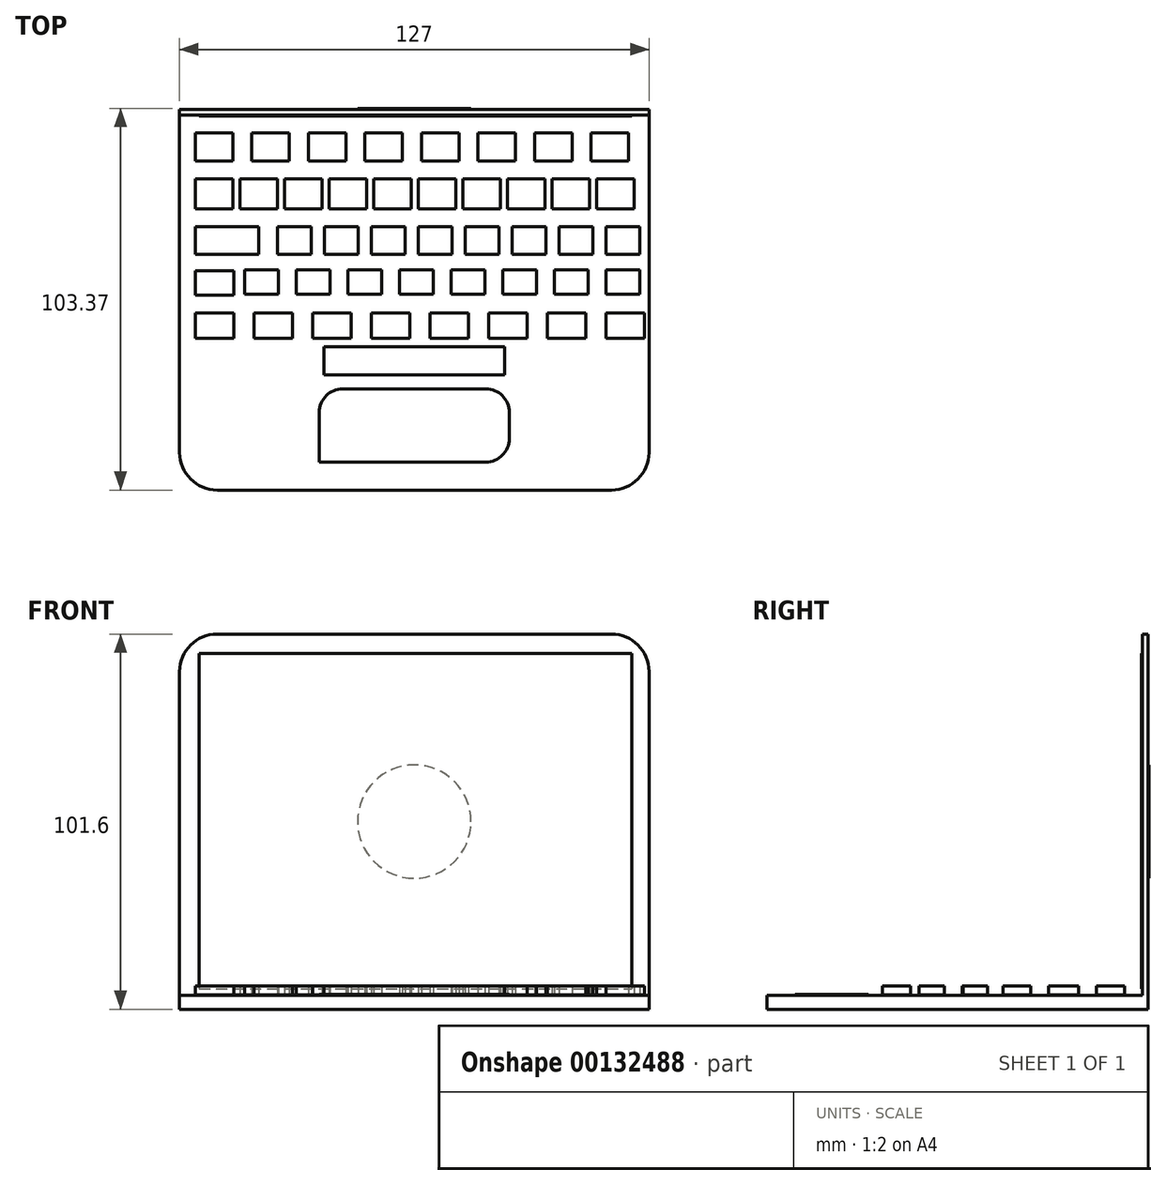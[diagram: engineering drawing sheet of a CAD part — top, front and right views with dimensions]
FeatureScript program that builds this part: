
annotation { "Feature Type Name" : "Feature", "Feature Type Description" : "" }
export const myFeature = defineFeature(function(context is Context, id is Id, definition is map)
    precondition{}
    {
        {
            var Q0;
            Q0=qCreatedBy(makeId("Front.planeOp"),FACE);
            var sketch = newSketch(context, id + "F0", { "sketchPlane" : qUnion([Q0])});
            skLineSegment(sketch, "E0.bottom", {"start": v(63.5, -50.8) * mm, "end": v(-63.5, -50.8) * mm});
            skLineSegment(sketch, "E0.top", {"start": v(63.5, 50.8) * mm, "end": v(-63.5, 50.8) * mm});
            skLineSegment(sketch, "E0.left", {"start": v(63.5, -50.8) * mm, "end": v(63.5, 50.8) * mm});
            skLineSegment(sketch, "E0.right", {"start": v(-63.5, -50.8) * mm, "end": v(-63.5, 50.8) * mm});
            skPoint(sketch, "E0.middle", {"position": v(0, 0) * mm});
            skSolve(sketch);
        }
        {
            var Q0;
            Q0 = qSketchRegion(id + "F0", true);
            extrude(context, id + "F1", {"entities" : qUnion([Q0]), "depth" : 1.52 * mm});
        }
        {
            var Q0;
            Q0=makeQuery(id+"F1.opExtrude","CAP_FACE",FACE,{"disambiguationData":[OSD([sQuery(id+"F0.wireOp",EDGE,"E0.bottom"),sQuery(id+"F0.wireOp",EDGE,"E0.top"),sQuery(id+"F0.wireOp",EDGE,"E0.left"),sQuery(id+"F0.wireOp",EDGE,"E0.right")])],"isStart":false});
            var sketch = newSketch(context, id + "F2", { "sketchPlane" : qUnion([Q0])});
            skLineSegment(sketch, "E1.bottom", {"start": v(-63.5, -50.8) * mm, "end": v(63.5, -50.8) * mm});
            skLineSegment(sketch, "E1.top", {"start": v(-63.5, -47) * mm, "end": v(63.5, -47) * mm});
            skLineSegment(sketch, "E1.left", {"start": v(-63.5, -50.8) * mm, "end": v(-63.5, -47) * mm});
            skLineSegment(sketch, "E1.right", {"start": v(63.5, -50.8) * mm, "end": v(63.5, -47) * mm});
            skSolve(sketch);
        }
        {
            var Q0;
            Q0 = qSketchRegion(id + "F2", true);
            extrude(context, id + "F3", {"entities" : qUnion([Q0]), "operationType" : NewBodyOperationType.ADD, "depth" : 101.6 * mm});
        }
        {
            var Q0;
            Q0=makeQuery(id+"F3.opExtrude","CAP_EDGE",EDGE,{"disambiguationData":[OSD([sQuery(id+"F2.wireOp",EDGE,"E1.left")])],"isStart":false});
            var Q1;
            Q1=makeQuery(id+"F3.opExtrude","CAP_EDGE",EDGE,{"disambiguationData":[OSD([sQuery(id+"F2.wireOp",EDGE,"E1.right")])],"isStart":false});
            var Q2;
            Q2=makeQuery(id+"F1.opExtrude","SWEPT_EDGE",EDGE,{"disambiguationData":[OSD([sQuery(id+"F0.wireOp",EDGE,"E0.top"),sQuery(id+"F0.wireOp",EDGE,"E0.right")])]});
            var Q3;
            Q3=makeQuery(id+"F1.opExtrude","SWEPT_EDGE",EDGE,{"disambiguationData":[OSD([sQuery(id+"F0.wireOp",EDGE,"E0.top"),sQuery(id+"F0.wireOp",EDGE,"E0.left")])]});
            fillet(context, id + "F4", {"entities" : qUnion([Q0, Q1, Q2, Q3]), "radius" : 10.16 * mm, "tangentPropagation" : true, "allowEdgeOverflow" : false});
        }
        {
            var Q0;
            Q0=makeQuery(id+"F1.opExtrude","CAP_FACE",FACE,{"disambiguationData":[OSD([sQuery(id+"F0.wireOp",EDGE,"E0.bottom"),sQuery(id+"F0.wireOp",EDGE,"E0.top"),sQuery(id+"F0.wireOp",EDGE,"E0.left"),sQuery(id+"F0.wireOp",EDGE,"E0.right")])],"isStart":false});
            var sketch = newSketch(context, id + "F5", { "sketchPlane" : qUnion([Q0])});
            skLineSegment(sketch, "E2.bottom", {"start": v(-58.24, 45.59) * mm, "end": v(58.8, 45.59) * mm});
            skLineSegment(sketch, "E2.top", {"start": v(-58.24, -45.21) * mm, "end": v(58.8, -45.21) * mm});
            skLineSegment(sketch, "E2.left", {"start": v(-58.24, 45.59) * mm, "end": v(-58.24, -45.21) * mm});
            skLineSegment(sketch, "E2.right", {"start": v(58.8, 45.59) * mm, "end": v(58.8, -45.21) * mm});
            skSolve(sketch);
        }
        {
            var Q0;
            Q0 = qSketchRegion(id + "F5", true);
            extrude(context, id + "F6", {"entities" : qUnion([Q0]), "depth" : 0.25 * mm});
        }
        {
            var Q0;
            Q0=makeQuery(id+"F3.opExtrude","SWEPT_FACE",FACE,{"disambiguationData":[OSD([sQuery(id+"F2.wireOp",EDGE,"E1.top")])]});
            var sketch = newSketch(context, id + "F7", { "sketchPlane" : qUnion([Q0])});
            skLineSegment(sketch, "E3.bottom", {"start": v(19.35, -95.54) * mm, "end": v(-25.7, -95.54) * mm});
            skLineSegment(sketch, "E3.top", {"start": v(19.35, -75.73) * mm, "end": v(-19.35, -75.73) * mm});
            skLineSegment(sketch, "E3.left", {"start": v(25.7, -89.2) * mm, "end": v(25.7, -82.08) * mm});
            skLineSegment(sketch, "E3.right", {"start": v(-25.7, -95.54) * mm, "end": v(-25.7, -82.08) * mm});
            skPoint(sketch, "E3.middle", {"position": v(0, -85.63) * mm});
            skPoint(sketch, "E4.visualSharp", {"position": v(-25.7, -75.73) * mm});
            skArc(sketch, "E4.filletArc", {"start": v(-19.35, -75.73) * mm, "mid": v(-23.84, -77.59) * mm, "end": v(-25.7, -82.08) * mm});
            skPoint(sketch, "E5.visualSharp", {"position": v(25.7, -75.73) * mm});
            skArc(sketch, "E5.filletArc", {"start": v(25.7, -82.08) * mm, "mid": v(23.84, -77.59) * mm, "end": v(19.35, -75.73) * mm});
            skPoint(sketch, "E6.visualSharp", {"position": v(25.7, -95.54) * mm});
            skArc(sketch, "E6.filletArc", {"start": v(19.35, -95.54) * mm, "mid": v(23.84, -93.68) * mm, "end": v(25.7, -89.2) * mm});
            skSolve(sketch);
        }
        {
            var Q0;
            Q0 = qSketchRegion(id + "F7", true);
            extrude(context, id + "F8", {"entities" : qUnion([Q0]), "depth" : 0.25 * mm});
        }
        {
            var Q0;
            Q0=makeQuery(id+"F3.opExtrude","SWEPT_FACE",FACE,{"disambiguationData":[OSD([sQuery(id+"F2.wireOp",EDGE,"E1.top")])]});
            var sketch = newSketch(context, id + "F9", { "sketchPlane" : qUnion([Q0])});
            skLineSegment(sketch, "E7.bottom", {"start": v(-49.14, -14.08) * mm, "end": v(-59.3, -14.08) * mm});
            skLineSegment(sketch, "E7.top", {"start": v(-49.14, -6.46) * mm, "end": v(-59.3, -6.46) * mm});
            skLineSegment(sketch, "E7.left", {"start": v(-49.14, -14.08) * mm, "end": v(-49.14, -6.46) * mm});
            skLineSegment(sketch, "E7.right", {"start": v(-59.3, -14.08) * mm, "end": v(-59.3, -6.46) * mm});
            skPoint(sketch, "E7.middle", {"position": v(-54.22, -10.27) * mm});
            skLineSegment(sketch, "E8.1.0.0", {"start": v(-33.84, -14.08) * mm, "end": v(-33.84, -6.46) * mm});
            skLineSegment(sketch, "E8.1.0.1", {"start": v(-33.84, -6.46) * mm, "end": v(-44, -6.46) * mm});
            skLineSegment(sketch, "E8.1.0.2", {"start": v(-44, -14.08) * mm, "end": v(-44, -6.46) * mm});
            skLineSegment(sketch, "E8.1.0.3", {"start": v(-33.84, -14.08) * mm, "end": v(-44, -14.08) * mm});
            skLineSegment(sketch, "E8.2.0.0", {"start": v(-18.53, -14.08) * mm, "end": v(-18.53, -6.46) * mm});
            skLineSegment(sketch, "E8.2.0.1", {"start": v(-18.53, -6.46) * mm, "end": v(-28.7, -6.46) * mm});
            skLineSegment(sketch, "E8.2.0.2", {"start": v(-28.7, -14.08) * mm, "end": v(-28.7, -6.46) * mm});
            skLineSegment(sketch, "E8.2.0.3", {"start": v(-18.53, -14.08) * mm, "end": v(-28.7, -14.08) * mm});
            skLineSegment(sketch, "E8.3.0.0", {"start": v(-3.23, -14.08) * mm, "end": v(-3.23, -6.46) * mm});
            skLineSegment(sketch, "E8.3.0.1", {"start": v(-3.23, -6.46) * mm, "end": v(-13.39, -6.46) * mm});
            skLineSegment(sketch, "E8.3.0.2", {"start": v(-13.39, -14.08) * mm, "end": v(-13.39, -6.46) * mm});
            skLineSegment(sketch, "E8.3.0.3", {"start": v(-3.23, -14.08) * mm, "end": v(-13.39, -14.08) * mm});
            skLineSegment(sketch, "E8.4.0.0", {"start": v(12.08, -14.08) * mm, "end": v(12.08, -6.46) * mm});
            skLineSegment(sketch, "E8.4.0.1", {"start": v(12.08, -6.46) * mm, "end": v(1.92, -6.46) * mm});
            skLineSegment(sketch, "E8.4.0.2", {"start": v(1.92, -14.08) * mm, "end": v(1.92, -6.46) * mm});
            skLineSegment(sketch, "E8.4.0.3", {"start": v(12.08, -14.08) * mm, "end": v(1.92, -14.08) * mm});
            skLineSegment(sketch, "E8.5.0.0", {"start": v(27.38, -14.08) * mm, "end": v(27.38, -6.46) * mm});
            skLineSegment(sketch, "E8.5.0.1", {"start": v(27.38, -6.46) * mm, "end": v(17.22, -6.46) * mm});
            skLineSegment(sketch, "E8.5.0.2", {"start": v(17.22, -14.08) * mm, "end": v(17.22, -6.46) * mm});
            skLineSegment(sketch, "E8.5.0.3", {"start": v(27.38, -14.08) * mm, "end": v(17.22, -14.08) * mm});
            skLineSegment(sketch, "E8.6.0.0", {"start": v(42.69, -14.08) * mm, "end": v(42.69, -6.46) * mm});
            skLineSegment(sketch, "E8.6.0.1", {"start": v(42.69, -6.46) * mm, "end": v(32.53, -6.46) * mm});
            skLineSegment(sketch, "E8.6.0.2", {"start": v(32.53, -14.08) * mm, "end": v(32.53, -6.46) * mm});
            skLineSegment(sketch, "E8.6.0.3", {"start": v(42.69, -14.08) * mm, "end": v(32.53, -14.08) * mm});
            skLineSegment(sketch, "E8.7.0.0", {"start": v(58, -14.08) * mm, "end": v(58, -6.46) * mm});
            skLineSegment(sketch, "E8.7.0.1", {"start": v(58, -6.46) * mm, "end": v(47.83, -6.46) * mm});
            skLineSegment(sketch, "E8.7.0.2", {"start": v(47.83, -14.08) * mm, "end": v(47.83, -6.46) * mm});
            skLineSegment(sketch, "E8.7.0.3", {"start": v(58, -14.08) * mm, "end": v(47.83, -14.08) * mm});
            skLineSegment(sketch, "E9.bottom", {"start": v(-49.14, -26.97) * mm, "end": v(-59.3, -26.97) * mm});
            skLineSegment(sketch, "E9.top", {"start": v(-49.14, -18.9) * mm, "end": v(-59.3, -18.9) * mm});
            skLineSegment(sketch, "E9.left", {"start": v(-49.14, -26.97) * mm, "end": v(-49.14, -18.9) * mm});
            skLineSegment(sketch, "E9.right", {"start": v(-59.3, -26.97) * mm, "end": v(-59.3, -18.9) * mm});
            skPoint(sketch, "E9.middle", {"position": v(-54.22, -22.94) * mm});
            skPoint(sketch, "E9.middle.positionSnap0", {"position": v(-54.22, -14.08) * mm});
            skPoint(sketch, "E9.centerSnap0", {"position": v(-54.22, -14.08) * mm});
            skLineSegment(sketch, "E10.bottom", {"start": v(24.5, -71.92) * mm, "end": v(-24.5, -71.92) * mm});
            skLineSegment(sketch, "E10.top", {"start": v(24.5, -64.26) * mm, "end": v(-24.5, -64.26) * mm});
            skLineSegment(sketch, "E10.left", {"start": v(24.5, -71.92) * mm, "end": v(24.5, -64.26) * mm});
            skLineSegment(sketch, "E10.right", {"start": v(-24.5, -71.92) * mm, "end": v(-24.5, -64.26) * mm});
            skPoint(sketch, "E10.middle", {"position": v(0, -68.1) * mm});
            skLineSegment(sketch, "E11.1.0.0", {"start": v(-37.08, -26.97) * mm, "end": v(-37.08, -18.9) * mm});
            skLineSegment(sketch, "E11.1.0.1", {"start": v(-37.08, -18.9) * mm, "end": v(-47.24, -18.9) * mm});
            skLineSegment(sketch, "E11.1.0.2", {"start": v(-47.24, -26.97) * mm, "end": v(-47.24, -18.9) * mm});
            skLineSegment(sketch, "E11.1.0.3", {"start": v(-37.08, -26.97) * mm, "end": v(-47.24, -26.97) * mm});
            skLineSegment(sketch, "E11.2.0.0", {"start": v(-25.01, -26.97) * mm, "end": v(-25.01, -18.9) * mm});
            skLineSegment(sketch, "E11.2.0.1", {"start": v(-25.01, -18.9) * mm, "end": v(-35.17, -18.9) * mm});
            skLineSegment(sketch, "E11.2.0.2", {"start": v(-35.17, -26.97) * mm, "end": v(-35.17, -18.9) * mm});
            skLineSegment(sketch, "E11.2.0.3", {"start": v(-25.01, -26.97) * mm, "end": v(-35.17, -26.97) * mm});
            skLineSegment(sketch, "E11.3.0.0", {"start": v(-12.95, -26.97) * mm, "end": v(-12.95, -18.9) * mm});
            skLineSegment(sketch, "E11.3.0.1", {"start": v(-12.95, -18.9) * mm, "end": v(-23.1, -18.9) * mm});
            skLineSegment(sketch, "E11.3.0.2", {"start": v(-23.1, -26.97) * mm, "end": v(-23.1, -18.9) * mm});
            skLineSegment(sketch, "E11.3.0.3", {"start": v(-12.95, -26.97) * mm, "end": v(-23.1, -26.97) * mm});
            skLineSegment(sketch, "E11.4.0.0", {"start": v(-0.88, -26.97) * mm, "end": v(-0.88, -18.9) * mm});
            skLineSegment(sketch, "E11.4.0.1", {"start": v(-0.88, -18.9) * mm, "end": v(-11.04, -18.9) * mm});
            skLineSegment(sketch, "E11.4.0.2", {"start": v(-11.04, -26.97) * mm, "end": v(-11.04, -18.9) * mm});
            skLineSegment(sketch, "E11.4.0.3", {"start": v(-0.88, -26.97) * mm, "end": v(-11.04, -26.97) * mm});
            skLineSegment(sketch, "E11.5.0.0", {"start": v(11.18, -26.97) * mm, "end": v(11.18, -18.9) * mm});
            skLineSegment(sketch, "E11.5.0.1", {"start": v(11.18, -18.9) * mm, "end": v(1.02, -18.9) * mm});
            skLineSegment(sketch, "E11.5.0.2", {"start": v(1.02, -26.97) * mm, "end": v(1.02, -18.9) * mm});
            skLineSegment(sketch, "E11.5.0.3", {"start": v(11.18, -26.97) * mm, "end": v(1.02, -26.97) * mm});
            skLineSegment(sketch, "E11.6.0.0", {"start": v(23.25, -26.97) * mm, "end": v(23.25, -18.9) * mm});
            skLineSegment(sketch, "E11.6.0.1", {"start": v(23.25, -18.9) * mm, "end": v(13.09, -18.9) * mm});
            skLineSegment(sketch, "E11.6.0.2", {"start": v(13.09, -26.97) * mm, "end": v(13.09, -18.9) * mm});
            skLineSegment(sketch, "E11.6.0.3", {"start": v(23.25, -26.97) * mm, "end": v(13.09, -26.97) * mm});
            skLineSegment(sketch, "E11.7.0.0", {"start": v(35.31, -26.97) * mm, "end": v(35.31, -18.9) * mm});
            skLineSegment(sketch, "E11.7.0.1", {"start": v(35.31, -18.9) * mm, "end": v(25.15, -18.9) * mm});
            skLineSegment(sketch, "E11.7.0.2", {"start": v(25.15, -26.97) * mm, "end": v(25.15, -18.9) * mm});
            skLineSegment(sketch, "E11.7.0.3", {"start": v(35.31, -26.97) * mm, "end": v(25.15, -26.97) * mm});
            skLineSegment(sketch, "E11.8.0.0", {"start": v(47.38, -26.97) * mm, "end": v(47.38, -18.9) * mm});
            skLineSegment(sketch, "E11.8.0.1", {"start": v(47.38, -18.9) * mm, "end": v(37.22, -18.9) * mm});
            skLineSegment(sketch, "E11.8.0.2", {"start": v(37.22, -26.97) * mm, "end": v(37.22, -18.9) * mm});
            skLineSegment(sketch, "E11.8.0.3", {"start": v(47.38, -26.97) * mm, "end": v(37.22, -26.97) * mm});
            skLineSegment(sketch, "E11.9.0.0", {"start": v(59.44, -26.97) * mm, "end": v(59.44, -18.9) * mm});
            skLineSegment(sketch, "E11.9.0.1", {"start": v(59.44, -18.9) * mm, "end": v(49.28, -18.9) * mm});
            skLineSegment(sketch, "E11.9.0.2", {"start": v(49.28, -26.97) * mm, "end": v(49.28, -18.9) * mm});
            skLineSegment(sketch, "E11.9.0.3", {"start": v(59.44, -26.97) * mm, "end": v(49.28, -26.97) * mm});
            skLineSegment(sketch, "E11.direction1", {"start": v(-49.14, -26.97) * mm, "end": v(-37.08, -26.97) * mm, "construction": true});
            skPoint(sketch, "E12.oppositeSnap0", {"position": v(-42.16, -18.9) * mm});
            skLineSegment(sketch, "E12.bottom", {"start": v(-59.3, -31.8) * mm, "end": v(-42.16, -31.8) * mm});
            skLineSegment(sketch, "E12.top", {"start": v(-59.3, -39.27) * mm, "end": v(-42.16, -39.27) * mm});
            skLineSegment(sketch, "E12.left", {"start": v(-59.3, -31.8) * mm, "end": v(-59.3, -39.27) * mm});
            skLineSegment(sketch, "E12.right", {"start": v(-42.16, -31.8) * mm, "end": v(-42.16, -39.27) * mm});
            skPoint(sketch, "E13.firstSnap0", {"position": v(-37.08, -22.94) * mm});
            skLineSegment(sketch, "E13.bottom", {"start": v(-37.08, -31.8) * mm, "end": v(-27.92, -31.8) * mm});
            skLineSegment(sketch, "E13.top", {"start": v(-37.08, -39.27) * mm, "end": v(-27.92, -39.27) * mm});
            skLineSegment(sketch, "E13.left", {"start": v(-37.08, -31.8) * mm, "end": v(-37.08, -39.27) * mm});
            skLineSegment(sketch, "E13.right", {"start": v(-27.92, -31.8) * mm, "end": v(-27.92, -39.27) * mm});
            skLineSegment(sketch, "E14.1.0.0", {"start": v(-24.38, -31.8) * mm, "end": v(-15.22, -31.8) * mm});
            skLineSegment(sketch, "E14.1.0.1", {"start": v(-15.22, -31.8) * mm, "end": v(-15.22, -39.27) * mm});
            skLineSegment(sketch, "E14.1.0.2", {"start": v(-24.38, -39.27) * mm, "end": v(-15.22, -39.27) * mm});
            skLineSegment(sketch, "E14.1.0.3", {"start": v(-24.38, -31.8) * mm, "end": v(-24.38, -39.27) * mm});
            skLineSegment(sketch, "E14.2.0.0", {"start": v(-11.68, -31.8) * mm, "end": v(-2.52, -31.8) * mm});
            skLineSegment(sketch, "E14.2.0.1", {"start": v(-2.52, -31.8) * mm, "end": v(-2.52, -39.27) * mm});
            skLineSegment(sketch, "E14.2.0.2", {"start": v(-11.68, -39.27) * mm, "end": v(-2.52, -39.27) * mm});
            skLineSegment(sketch, "E14.2.0.3", {"start": v(-11.68, -31.8) * mm, "end": v(-11.68, -39.27) * mm});
            skLineSegment(sketch, "E14.3.0.0", {"start": v(1.02, -31.8) * mm, "end": v(10.18, -31.8) * mm});
            skLineSegment(sketch, "E14.3.0.1", {"start": v(10.18, -31.8) * mm, "end": v(10.18, -39.27) * mm});
            skLineSegment(sketch, "E14.3.0.2", {"start": v(1.02, -39.27) * mm, "end": v(10.18, -39.27) * mm});
            skLineSegment(sketch, "E14.3.0.3", {"start": v(1.02, -31.8) * mm, "end": v(1.02, -39.27) * mm});
            skLineSegment(sketch, "E14.4.0.0", {"start": v(13.72, -31.8) * mm, "end": v(22.88, -31.8) * mm});
            skLineSegment(sketch, "E14.4.0.1", {"start": v(22.88, -31.8) * mm, "end": v(22.88, -39.27) * mm});
            skLineSegment(sketch, "E14.4.0.2", {"start": v(13.72, -39.27) * mm, "end": v(22.88, -39.27) * mm});
            skLineSegment(sketch, "E14.4.0.3", {"start": v(13.72, -31.8) * mm, "end": v(13.72, -39.27) * mm});
            skLineSegment(sketch, "E14.5.0.0", {"start": v(26.42, -31.8) * mm, "end": v(35.58, -31.8) * mm});
            skLineSegment(sketch, "E14.5.0.1", {"start": v(35.58, -31.8) * mm, "end": v(35.58, -39.27) * mm});
            skLineSegment(sketch, "E14.5.0.2", {"start": v(26.42, -39.27) * mm, "end": v(35.58, -39.27) * mm});
            skLineSegment(sketch, "E14.5.0.3", {"start": v(26.42, -31.8) * mm, "end": v(26.42, -39.27) * mm});
            skLineSegment(sketch, "E14.6.0.0", {"start": v(39.12, -31.8) * mm, "end": v(48.28, -31.8) * mm});
            skLineSegment(sketch, "E14.6.0.1", {"start": v(48.28, -31.8) * mm, "end": v(48.28, -39.27) * mm});
            skLineSegment(sketch, "E14.6.0.2", {"start": v(39.12, -39.27) * mm, "end": v(48.28, -39.27) * mm});
            skLineSegment(sketch, "E14.6.0.3", {"start": v(39.12, -31.8) * mm, "end": v(39.12, -39.27) * mm});
            skLineSegment(sketch, "E14.7.0.0", {"start": v(51.82, -31.8) * mm, "end": v(60.98, -31.8) * mm});
            skLineSegment(sketch, "E14.7.0.1", {"start": v(60.98, -31.8) * mm, "end": v(60.98, -39.27) * mm});
            skLineSegment(sketch, "E14.7.0.2", {"start": v(51.82, -39.27) * mm, "end": v(60.98, -39.27) * mm});
            skLineSegment(sketch, "E14.7.0.3", {"start": v(51.82, -31.8) * mm, "end": v(51.82, -39.27) * mm});
            skLineSegment(sketch, "E14.direction1", {"start": v(-37.08, -31.8) * mm, "end": v(-24.38, -31.8) * mm, "construction": true});
            skLineSegment(sketch, "E15.bottom", {"start": v(-59.3, -43.7) * mm, "end": v(-48.89, -43.7) * mm});
            skLineSegment(sketch, "E15.top", {"start": v(-59.3, -50.35) * mm, "end": v(-48.89, -50.35) * mm});
            skLineSegment(sketch, "E15.left", {"start": v(-59.3, -43.7) * mm, "end": v(-59.3, -50.35) * mm});
            skLineSegment(sketch, "E15.right", {"start": v(-48.89, -43.7) * mm, "end": v(-48.89, -50.35) * mm});
            skLineSegment(sketch, "E16.bottom", {"start": v(60.98, -43.5) * mm, "end": v(51.82, -43.5) * mm});
            skLineSegment(sketch, "E16.top", {"start": v(60.98, -50.15) * mm, "end": v(51.82, -50.15) * mm});
            skLineSegment(sketch, "E16.left", {"start": v(60.98, -43.5) * mm, "end": v(60.98, -50.15) * mm});
            skLineSegment(sketch, "E16.right", {"start": v(51.82, -43.5) * mm, "end": v(51.82, -50.15) * mm});
            skLineSegment(sketch, "E17.1.0.0", {"start": v(47, -43.5) * mm, "end": v(37.85, -43.5) * mm});
            skLineSegment(sketch, "E17.1.0.1", {"start": v(47, -43.5) * mm, "end": v(47, -50.15) * mm});
            skLineSegment(sketch, "E17.1.0.2", {"start": v(47, -50.15) * mm, "end": v(37.85, -50.15) * mm});
            skLineSegment(sketch, "E17.1.0.3", {"start": v(37.85, -43.5) * mm, "end": v(37.85, -50.15) * mm});
            skLineSegment(sketch, "E17.2.0.0", {"start": v(33.04, -43.5) * mm, "end": v(23.88, -43.5) * mm});
            skLineSegment(sketch, "E17.2.0.1", {"start": v(33.04, -43.5) * mm, "end": v(33.04, -50.15) * mm});
            skLineSegment(sketch, "E17.2.0.2", {"start": v(33.04, -50.15) * mm, "end": v(23.88, -50.15) * mm});
            skLineSegment(sketch, "E17.2.0.3", {"start": v(23.88, -43.5) * mm, "end": v(23.88, -50.15) * mm});
            skLineSegment(sketch, "E17.3.0.0", {"start": v(19.07, -43.5) * mm, "end": v(9.91, -43.5) * mm});
            skLineSegment(sketch, "E17.3.0.1", {"start": v(19.07, -43.5) * mm, "end": v(19.07, -50.15) * mm});
            skLineSegment(sketch, "E17.3.0.2", {"start": v(19.07, -50.15) * mm, "end": v(9.91, -50.15) * mm});
            skLineSegment(sketch, "E17.3.0.3", {"start": v(9.91, -43.5) * mm, "end": v(9.91, -50.15) * mm});
            skLineSegment(sketch, "E17.4.0.0", {"start": v(5.1, -43.5) * mm, "end": v(-4.06, -43.5) * mm});
            skLineSegment(sketch, "E17.4.0.1", {"start": v(5.1, -43.5) * mm, "end": v(5.1, -50.15) * mm});
            skLineSegment(sketch, "E17.4.0.2", {"start": v(5.1, -50.15) * mm, "end": v(-4.06, -50.15) * mm});
            skLineSegment(sketch, "E17.4.0.3", {"start": v(-4.06, -43.5) * mm, "end": v(-4.06, -50.15) * mm});
            skLineSegment(sketch, "E17.5.0.0", {"start": v(-8.87, -43.5) * mm, "end": v(-18.03, -43.5) * mm});
            skLineSegment(sketch, "E17.5.0.1", {"start": v(-8.87, -43.5) * mm, "end": v(-8.87, -50.15) * mm});
            skLineSegment(sketch, "E17.5.0.2", {"start": v(-8.87, -50.15) * mm, "end": v(-18.03, -50.15) * mm});
            skLineSegment(sketch, "E17.5.0.3", {"start": v(-18.03, -43.5) * mm, "end": v(-18.03, -50.15) * mm});
            skLineSegment(sketch, "E17.6.0.0", {"start": v(-22.84, -43.5) * mm, "end": v(-32, -43.5) * mm});
            skLineSegment(sketch, "E17.6.0.1", {"start": v(-22.84, -43.5) * mm, "end": v(-22.84, -50.15) * mm});
            skLineSegment(sketch, "E17.6.0.2", {"start": v(-22.84, -50.15) * mm, "end": v(-32, -50.15) * mm});
            skLineSegment(sketch, "E17.6.0.3", {"start": v(-32, -43.5) * mm, "end": v(-32, -50.15) * mm});
            skLineSegment(sketch, "E17.7.0.0", {"start": v(-36.81, -43.5) * mm, "end": v(-45.97, -43.5) * mm});
            skLineSegment(sketch, "E17.7.0.1", {"start": v(-36.81, -43.5) * mm, "end": v(-36.81, -50.15) * mm});
            skLineSegment(sketch, "E17.7.0.2", {"start": v(-36.81, -50.15) * mm, "end": v(-45.97, -50.15) * mm});
            skLineSegment(sketch, "E17.7.0.3", {"start": v(-45.97, -43.5) * mm, "end": v(-45.97, -50.15) * mm});
            skLineSegment(sketch, "E18.bottom", {"start": v(-59.3, -55.2) * mm, "end": v(-48.89, -55.2) * mm});
            skLineSegment(sketch, "E18.top", {"start": v(-59.3, -62.05) * mm, "end": v(-48.89, -62.05) * mm});
            skLineSegment(sketch, "E18.left", {"start": v(-59.3, -55.2) * mm, "end": v(-59.3, -62.05) * mm});
            skLineSegment(sketch, "E18.right", {"start": v(-48.89, -55.2) * mm, "end": v(-48.89, -62.05) * mm});
            skLineSegment(sketch, "E19.1.0.0", {"start": v(-43.43, -55.2) * mm, "end": v(-43.43, -62.05) * mm});
            skLineSegment(sketch, "E19.1.0.1", {"start": v(-43.43, -55.2) * mm, "end": v(-33.01, -55.2) * mm});
            skLineSegment(sketch, "E19.1.0.2", {"start": v(-33.01, -55.2) * mm, "end": v(-33.01, -62.05) * mm});
            skLineSegment(sketch, "E19.1.0.3", {"start": v(-43.43, -62.05) * mm, "end": v(-33.01, -62.05) * mm});
            skLineSegment(sketch, "E19.2.0.0", {"start": v(-27.55, -55.2) * mm, "end": v(-27.55, -62.05) * mm});
            skLineSegment(sketch, "E19.2.0.1", {"start": v(-27.55, -55.2) * mm, "end": v(-17.14, -55.2) * mm});
            skLineSegment(sketch, "E19.2.0.2", {"start": v(-17.14, -55.2) * mm, "end": v(-17.14, -62.05) * mm});
            skLineSegment(sketch, "E19.2.0.3", {"start": v(-27.55, -62.05) * mm, "end": v(-17.14, -62.05) * mm});
            skLineSegment(sketch, "E19.3.0.0", {"start": v(-11.68, -55.2) * mm, "end": v(-11.68, -62.05) * mm});
            skLineSegment(sketch, "E19.3.0.1", {"start": v(-11.68, -55.2) * mm, "end": v(-1.26, -55.2) * mm});
            skLineSegment(sketch, "E19.3.0.2", {"start": v(-1.26, -55.2) * mm, "end": v(-1.26, -62.05) * mm});
            skLineSegment(sketch, "E19.3.0.3", {"start": v(-11.68, -62.05) * mm, "end": v(-1.26, -62.05) * mm});
            skLineSegment(sketch, "E19.4.0.0", {"start": v(4.2, -55.2) * mm, "end": v(4.2, -62.05) * mm});
            skLineSegment(sketch, "E19.4.0.1", {"start": v(4.2, -55.2) * mm, "end": v(14.61, -55.2) * mm});
            skLineSegment(sketch, "E19.4.0.2", {"start": v(14.61, -55.2) * mm, "end": v(14.61, -62.05) * mm});
            skLineSegment(sketch, "E19.4.0.3", {"start": v(4.2, -62.05) * mm, "end": v(14.61, -62.05) * mm});
            skLineSegment(sketch, "E19.5.0.0", {"start": v(20.07, -55.2) * mm, "end": v(20.07, -62.05) * mm});
            skLineSegment(sketch, "E19.5.0.1", {"start": v(20.07, -55.2) * mm, "end": v(30.49, -55.2) * mm});
            skLineSegment(sketch, "E19.5.0.2", {"start": v(30.49, -55.2) * mm, "end": v(30.49, -62.05) * mm});
            skLineSegment(sketch, "E19.5.0.3", {"start": v(20.07, -62.05) * mm, "end": v(30.49, -62.05) * mm});
            skLineSegment(sketch, "E19.6.0.0", {"start": v(35.95, -55.2) * mm, "end": v(35.95, -62.05) * mm});
            skLineSegment(sketch, "E19.6.0.1", {"start": v(35.95, -55.2) * mm, "end": v(46.36, -55.2) * mm});
            skLineSegment(sketch, "E19.6.0.2", {"start": v(46.36, -55.2) * mm, "end": v(46.36, -62.05) * mm});
            skLineSegment(sketch, "E19.6.0.3", {"start": v(35.95, -62.05) * mm, "end": v(46.36, -62.05) * mm});
            skLineSegment(sketch, "E19.7.0.0", {"start": v(51.82, -55.2) * mm, "end": v(51.82, -62.05) * mm});
            skLineSegment(sketch, "E19.7.0.1", {"start": v(51.82, -55.2) * mm, "end": v(62.24, -55.2) * mm});
            skLineSegment(sketch, "E19.7.0.2", {"start": v(62.24, -55.2) * mm, "end": v(62.24, -62.05) * mm});
            skLineSegment(sketch, "E19.7.0.3", {"start": v(51.82, -62.05) * mm, "end": v(62.24, -62.05) * mm});
            skSolve(sketch);
        }
        {
            var Q0;
            Q0 = qSketchRegion(id + "F9", true);
            extrude(context, id + "F10", {"entities" : qUnion([Q0]), "depth" : 0.03 * mm});
        }
        {
            var Q0;
            Q0=makeQuery(id+"F1.opExtrude","CAP_FACE",FACE,{"disambiguationData":[OSD([sQuery(id+"F0.wireOp",EDGE,"E0.bottom"),sQuery(id+"F0.wireOp",EDGE,"E0.top"),sQuery(id+"F0.wireOp",EDGE,"E0.left"),sQuery(id+"F0.wireOp",EDGE,"E0.right")])],"isStart":true});
            var sketch = newSketch(context, id + "F11", { "sketchPlane" : qUnion([Q0])});
            skSolve(sketch);
        }
        {
            var Q0;
            Q0 = qSketchRegion(id + "F9", true);
            extrude(context, id + "F12", {"entities" : qUnion([Q0]), "depth" : 2.54 * mm});
        }
        {
            var Q0;
            {var subQ3=sQuery(id+"F0.wireOp",EDGE,"E0.bottom");Q0=makeQuery(id+"F11.imprint","IMPRINT",FACE,{"disambiguationData":[TD([[makeQuery(id+"F11.imprint","IMPRINT",EDGE,{"derivedFrom":makeQuery(id+"F1.opExtrude","CAP_EDGE",EDGE,{"disambiguationData":[OSD([subQ3])],"isStart":true})}),1.0]])]});}
            var sketch = newSketch(context, id + "F13", { "sketchPlane" : qUnion([Q0])});
            skCircle(sketch, "E20", {"center": v(0, 0) * mm, "radius": 15.33 * mm});
            skSolve(sketch);
        }
        {
            var Q0;
            Q0 = qSketchRegion(id + "F13", true);
            extrude(context, id + "F14", {"entities" : qUnion([Q0]), "operationType" : NewBodyOperationType.ADD, "depth" : 0.25 * mm});
        }
    });
